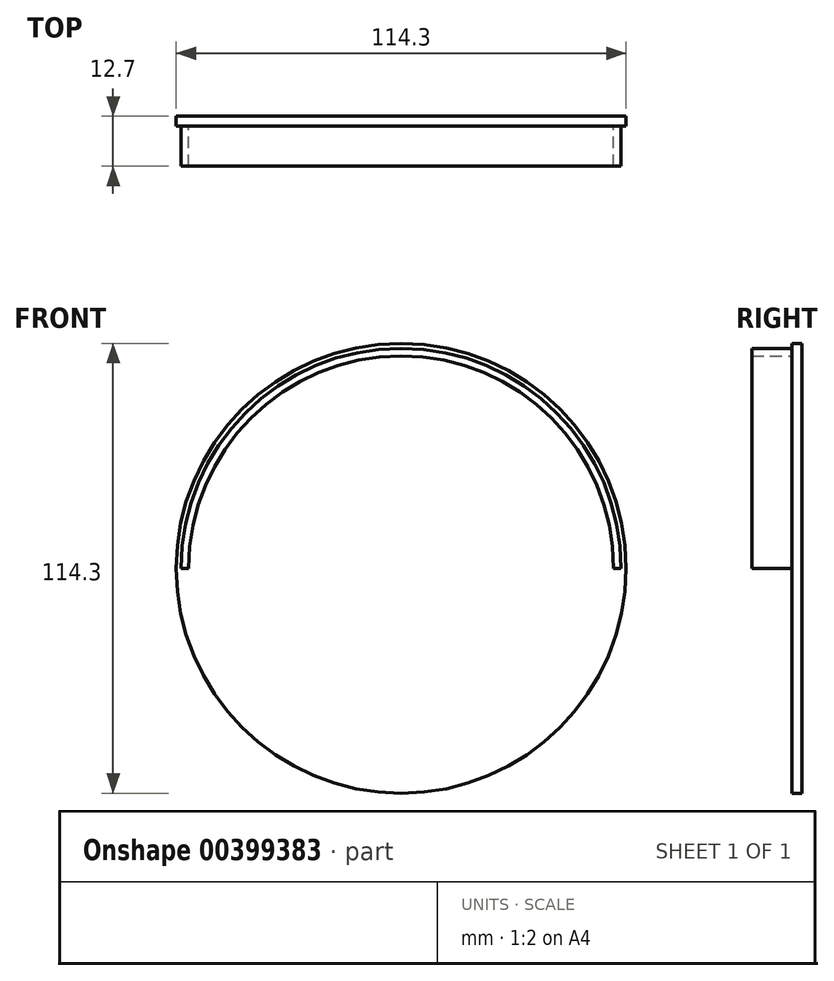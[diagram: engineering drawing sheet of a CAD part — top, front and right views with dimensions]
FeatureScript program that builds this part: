
annotation { "Feature Type Name" : "Feature", "Feature Type Description" : "" }
export const myFeature = defineFeature(function(context is Context, id is Id, definition is map)
    precondition{}
    {
        {
            var Q0;
            Q0=qCreatedBy(makeId("Front.planeOp"),FACE);
            var sketch = newSketch(context, id + "F0", { "sketchPlane" : qUnion([Q0])});
            skCircle(sketch, "E0", {"center": v(0, 0) * mm, "radius": 57.15 * mm});
            skSolve(sketch);
        }
        {
            var Q0;
            Q0 = qSketchRegion(id + "F0", true);
            extrude(context, id + "F1", {"entities" : qUnion([Q0]), "depth" : 2.54 * mm});
        }
        {
            var Q0;
            Q0=qCreatedBy(makeId("Front.planeOp"),FACE);
            var sketch = newSketch(context, id + "F2", { "sketchPlane" : qUnion([Q0])});
            skArc(sketch, "E1", {"start": v(53.98, 0) * mm, "mid": v(0, 53.98) * mm, "end": v(-53.98, 0) * mm});
            skArc(sketch, "E2", {"start": v(55.88, 0) * mm, "mid": v(0, 55.88) * mm, "end": v(-55.88, 0) * mm});
            skLineSegment(sketch, "E3", {"start": v(-55.88, 0) * mm, "end": v(-53.98, 0) * mm});
            skLineSegment(sketch, "E4", {"start": v(53.98, 0) * mm, "end": v(55.88, 0) * mm});
            skSolve(sketch);
        }
        {
            var Q0;
            Q0 = qSketchRegion(id + "F2", true);
            extrude(context, id + "F3", {"entities" : qUnion([Q0]), "operationType" : NewBodyOperationType.ADD, "depth" : 12.7 * mm});
        }
    });
